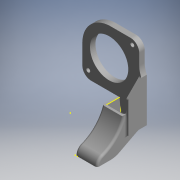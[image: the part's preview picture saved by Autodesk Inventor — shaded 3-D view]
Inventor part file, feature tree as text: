
AUTODESK INVENTOR PART (.ipt)
format: ipt  version: 2016 (Build 200138000, 138)  size: 1,054,208 bytes
history: native  units: mm (DEFAULTED — no unit token found)
features: sketch x6, fillet x5, other x3, projected_geometry x3, extrude x2, plane x2, hole x1, chamfer x1
ambient origin geometry x8: Origin, YZ Plane, XZ Plane, XY Plane, X Axis, Y Axis, Z Axis, Center Point
bodies: Solid1 (feature_tree)
feature tree (23):
  other  "new wind guide3.iam"
  other  "base.ipt:1"
  other  "guide.ipt:1"
  extrude  "Extrusion1"  Depth=2.0mm
  fillet  "Fillet1"  Radius=2.0mm
  fillet  "Fillet2"  Radius=2.0mm
  fillet  "Fillet4"  Radius=1.59mm
  extrude  "Extrusion2"  Depth=2.0mm TaperAngle=0.0deg
  hole  "Hole1"  [1 undecoded]
  fillet  "Fillet6"  Radius=2.0mm
  chamfer  "Chamfer1"  [1 undecoded]
  fillet  "Fillet7"  [1 undecoded]
  plane  "Work Plane1"
  sketch  "Sketch2"  dims[d0=10.0mm d1=40.0mm d2=2.0mm d3=0.0mm d4=2.0mm d5=1.59mm]
  sketch  "Sketch4"  dims[d7=20.0mm d9=2.0mm d10=0.0mm]
  sketch  "Sketch5"  dims[d11=6.0mm d12=6.0mm d13=4.0mm d14=2.0mm d15=90.0deg d16=2.0mm d17=20.594885mm d18=50.0mm]
  plane  "Work Plane1_1"
  sketch  "Sketch6"  dims[d19=11.75mm d20=2.0mm d21=45.0deg d22=2.0mm]
  projected_geometry  "Projected Loop1"
  sketch  "Sketch7"
  projected_geometry  "Projected Loop2"
  sketch  "Sketch8"
  projected_geometry  "Projected Loop3"
note: 3 required parameter values undecoded (feature->parameter linkage not recoverable at this tier; creation-order binding heuristic only, values carry confidence <= 0.55)
